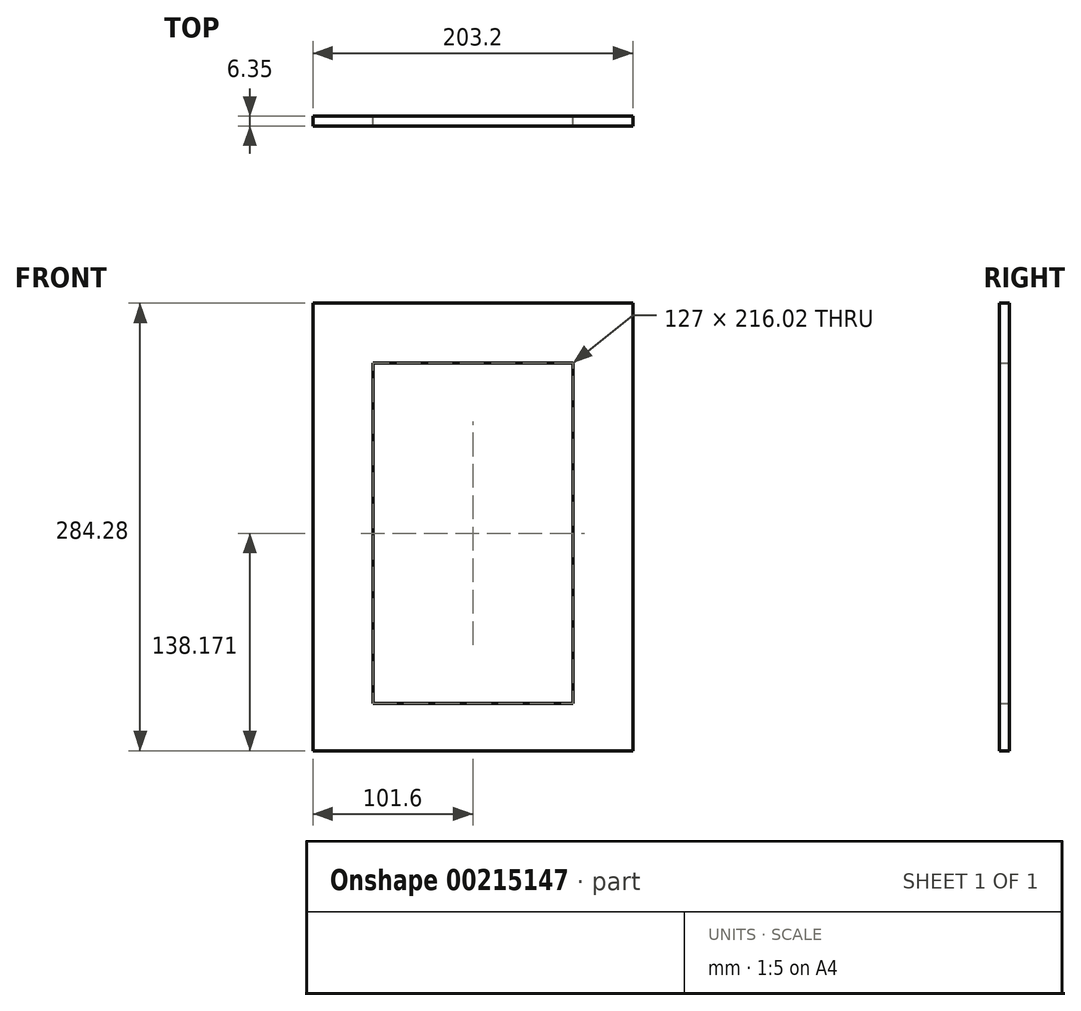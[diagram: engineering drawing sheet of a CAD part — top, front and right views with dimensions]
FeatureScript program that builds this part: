
annotation { "Feature Type Name" : "Feature", "Feature Type Description" : "" }
export const myFeature = defineFeature(function(context is Context, id is Id, definition is map)
    precondition{}
    {
        {
            var Q0;
            Q0=qCreatedBy(makeId("Front.planeOp"),FACE);
            var sketch = newSketch(context, id + "F0", { "sketchPlane" : qUnion([Q0])});
            skLineSegment(sketch, "E0.bottom", {"start": v(101.6, -129.44) * mm, "end": v(-101.6, -129.44) * mm});
            skLineSegment(sketch, "E0.top", {"start": v(101.6, 129.44) * mm, "end": v(-101.6, 129.44) * mm});
            skLineSegment(sketch, "E0.left", {"start": v(101.6, -129.44) * mm, "end": v(101.6, 129.44) * mm});
            skLineSegment(sketch, "E0.right", {"start": v(-101.6, -129.44) * mm, "end": v(-101.6, 129.44) * mm});
            skPoint(sketch, "E0.middle", {"position": v(0, 0) * mm});
            skLineSegment(sketch, "E1", {"start": v(-76.2, -129.44) * mm, "end": v(-76.2, 104.04) * mm});
            skLineSegment(sketch, "E2", {"start": v(-76.2, 104.04) * mm, "end": v(76.2, 104.04) * mm});
            skLineSegment(sketch, "E3", {"start": v(76.2, 104.04) * mm, "end": v(76.2, -129.44) * mm});
            skLineSegment(sketch, "E4.bottom", {"start": v(-101.6, -129.44) * mm, "end": v(101.6, -129.44) * mm});
            skLineSegment(sketch, "E4.top", {"start": v(-101.6, -154.84) * mm, "end": v(101.6, -154.84) * mm});
            skLineSegment(sketch, "E4.left", {"start": v(-101.6, -129.44) * mm, "end": v(-101.6, -154.84) * mm});
            skLineSegment(sketch, "E4.right", {"start": v(101.6, -129.44) * mm, "end": v(101.6, -154.84) * mm});
            skLineSegment(sketch, "E5", {"start": v(-63.5, -129.44) * mm, "end": v(-63.5, 104.04) * mm});
            skLineSegment(sketch, "E6", {"start": v(63.5, 104.04) * mm, "end": v(63.5, -129.44) * mm});
            skLineSegment(sketch, "E7", {"start": v(-63.5, -124.68) * mm, "end": v(63.5, -124.68) * mm});
            skLineSegment(sketch, "E8", {"start": v(-63.5, 91.34) * mm, "end": v(63.5, 91.34) * mm});
            skSolve(sketch);
        }
        {
            var Q0;
            Q0=makeQuery(id+"F0.imprint","IMPRINT",FACE,{"disambiguationData":[TD([[makeQuery(id+"F0.imprint","IMPRINT",EDGE,{"derivedFrom":sQuery(id+"F0.wireOp",EDGE,"E0.top")}),1.0]])]});
            var Q1;
            Q1=makeQuery(id+"F0.imprint","IMPRINT",FACE,{"disambiguationData":[TD([[makeQuery(id+"F0.imprint","IMPRINT",EDGE,{"derivedFrom":sQuery(id+"F0.wireOp",EDGE,"E4.top")}),1.0]])]});
            var Q2;
            {var subQ5=sQuery(id+"F0.wireOp",EDGE,"E8");Q2=makeQuery(id+"F0.imprint","IMPRINT",FACE,{"disambiguationData":[TD([[makeQuery(id+"F0.imprint","IMPRINT",EDGE,{"derivedFrom":subQ5}),1.0]])]});}
            var Q3;
            {var subQ1=sQuery(id+"F0.wireOp",EDGE,"E1");Q3=makeQuery(id+"F0.imprint","IMPRINT",FACE,{"disambiguationData":[TD([[makeQuery(id+"F0.imprint","IMPRINT",EDGE,{"derivedFrom":subQ1}),-1.0]])]});}
            var Q4;
            {var subQ1=sQuery(id+"F0.wireOp",EDGE,"E3");Q4=makeQuery(id+"F0.imprint","IMPRINT",FACE,{"disambiguationData":[TD([[makeQuery(id+"F0.imprint","IMPRINT",EDGE,{"derivedFrom":subQ1}),-1.0]])]});}
            var Q5;
            {var subQ5=sQuery(id+"F0.wireOp",EDGE,"E7");Q5=makeQuery(id+"F0.imprint","IMPRINT",FACE,{"disambiguationData":[TD([[makeQuery(id+"F0.imprint","IMPRINT",EDGE,{"derivedFrom":subQ5}),-1.0]])]});}
            extrude(context, id + "F1", {"entities" : qUnion([Q0, Q1, Q2, Q3, Q4, Q5]), "depth" : 6.35 * mm});
        }
    });
